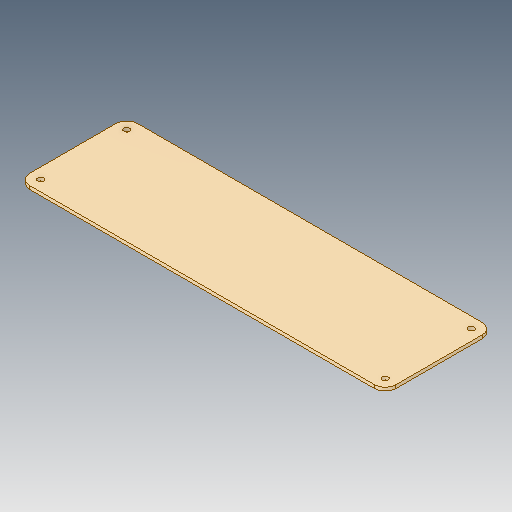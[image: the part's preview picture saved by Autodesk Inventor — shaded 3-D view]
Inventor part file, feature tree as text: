
AUTODESK INVENTOR PART (.ipt)
format: ipt  version: 2018 (Build 220112000, 112)  size: 109,056 bytes
history: native  units: in
note: dims shown in document units (in); Inventor stores cm internally (conversion verified against a paired STEP export)
features: mirror x2, sketch x2, other x1, extrude x1, fillet x1, hole x1, projected_geometry x1
ambient origin geometry x8: Origin, YZ Plane, XZ Plane, XY Plane, X Axis, Y Axis, Z Axis, Center Point
bodies: Solid1 (feature_tree)
feature tree (9):
  other  "<userpath>\OneDrive\projects\sPhenixTileTestStand\sPhenixTileTestStand.xlsx"
  extrude  "Extrusion1"  Depth=3.937in
  fillet  "Fillet1"  Radius=0.123in
  hole  "Hole1"  [1 undecoded]
  mirror  "Mirror1"
  mirror  "Mirror2"
  sketch  "Sketch1"  dims[d0=13.3858in d1=3.937in d2=0.123in]
  sketch  "Sketch2"  dims[d3=0.0in d4=0.3937in d6=0.3937in d7=0.217in d8=0.75in d9=0.394in d10=0.197in d11=90.0deg d12=1.0in d13=0.8108in d14=0.3937in]
  projected_geometry  "Projected Loop1"
note: 1 required parameter value undecoded (feature->parameter linkage not recoverable at this tier; creation-order binding heuristic only, values carry confidence <= 0.55)
